FCSTD DOCUMENT  (FreeCAD 0.19R23258 (Git))
Label: star_sketch
License: All rights reserved
LicenseURL: http://en.wikipedia.org/wiki/All_rights_reserved
objects: Sketcher::SketchObject×2
note: 2 computed .brp shape members not serialized (recipe doc carries the construction recipe); baked Part::Feature solids carry a one-line shape summary decoded from their .brp

FEATURE [Sketcher::SketchObject] Sketch
  sketch-geometry (31):
    g0: LineSegment [constr] StartX=0 StartY=15.4617 StartZ=0 EndX=-14.705 EndY=4.77794 EndZ=0
    g1: LineSegment [constr] StartX=-14.705 StartY=4.77794 StartZ=0 EndX=-9.08818 EndY=-12.5088 EndZ=0
    g2: LineSegment [constr] StartX=-9.08818 StartY=-12.5088 StartZ=0 EndX=9.08818 EndY=-12.5088 EndZ=0
    g3: LineSegment [constr] StartX=9.08818 StartY=-12.5088 StartZ=0 EndX=14.705 EndY=4.77794 EndZ=0
    g4: LineSegment [constr] StartX=14.705 StartY=4.77794 StartZ=0 EndX=0 EndY=15.4617 EndZ=0
    g5: Circle [constr] CenterX=0 CenterY=0 CenterZ=0 NormalX=0 NormalY=0 NormalZ=1 AngleXU=0 Radius=15.4617
    g6: LineSegment [constr] StartX=0 StartY=0 StartZ=0 EndX=0 EndY=40 EndZ=0
    g7: LineSegment [constr] StartX=0 StartY=0 StartZ=0 EndX=38.0423 EndY=12.3607 EndZ=0
    g8: LineSegment [constr] StartX=0 StartY=0 StartZ=0 EndX=23.5114 EndY=-32.3607 EndZ=0
    g9: LineSegment [constr] StartX=0 StartY=0 StartZ=0 EndX=-23.5114 EndY=-32.3607 EndZ=0
    g10: LineSegment [constr] StartX=0 StartY=0 StartZ=0 EndX=-38.0423 EndY=12.3607 EndZ=0
    g11: LineSegment StartX=0 StartY=40 StartZ=0 EndX=10.6055 EndY=14.5972 EndZ=0
    g12: LineSegment StartX=0 StartY=40 StartZ=0 EndX=-10.6055 EndY=14.5972 EndZ=0
    g13: LineSegment StartX=-38.0423 StartY=12.3607 StartZ=0 EndX=-17.1601 EndY=-5.57564 EndZ=0
    g14: LineSegment StartX=-38.0423 StartY=12.3607 StartZ=0 EndX=-10.6055 EndY=14.5972 EndZ=0
    g15: LineSegment StartX=-23.5114 StartY=-32.3607 StartZ=0 EndX=0 EndY=-18.0432 EndZ=0
    g16: LineSegment StartX=-14.705 StartY=4.77794 StartZ=0 EndX=-15.2847 EndY=2.3333 EndZ=0
    g17: LineSegment StartX=23.5114 StartY=-32.3607 StartZ=0 EndX=17.1601 EndY=-5.57564 EndZ=0
    g18: LineSegment StartX=23.5114 StartY=-32.3607 StartZ=0 EndX=0 EndY=-18.0432 EndZ=0
    g19: LineSegment StartX=0 StartY=15.4617 StartZ=0 EndX=2.50412 EndY=15.2576 EndZ=0
    g20: LineSegment StartX=38.0423 StartY=12.3607 StartZ=0 EndX=17.1601 EndY=-5.57564 EndZ=0
    g21: LineSegment StartX=-13.737 StartY=7.09642 StartZ=0 EndX=-14.705 EndY=4.77794 EndZ=0
    g22: LineSegment StartX=-2.50412 StartY=15.2576 StartZ=0 EndX=0 EndY=15.4617 EndZ=0
    g23: LineSegment StartX=-17.1601 StartY=-5.57564 StartZ=0 EndX=-23.5114 EndY=-32.3607 EndZ=0
    g24: LineSegment StartX=-10.9941 StartY=-10.8718 StartZ=0 EndX=-9.08818 EndY=-12.5088 EndZ=0
    g25: LineSegment StartX=-6.94232 StartY=-13.8155 StartZ=0 EndX=-9.08818 EndY=-12.5088 EndZ=0
    g26: LineSegment StartX=6.94232 StartY=-13.8155 StartZ=0 EndX=9.08818 EndY=-12.5088 EndZ=0
    g27: LineSegment StartX=10.9941 StartY=-10.8718 StartZ=0 EndX=9.08818 EndY=-12.5088 EndZ=0
    g28: LineSegment StartX=10.6055 StartY=14.5972 StartZ=0 EndX=38.0423 EndY=12.3607 EndZ=0
    g29: LineSegment StartX=15.2847 StartY=2.3333 StartZ=0 EndX=14.705 EndY=4.77794 EndZ=0
    g30: LineSegment StartX=13.737 StartY=7.09642 StartZ=0 EndX=14.705 EndY=4.77794 EndZ=0
  constraints (73):
    c: Coincident(g0,g1)
    c: Coincident(g1,g2)
    c: Coincident(g2,g3)
    c: Coincident(g3,g4)
    c: Coincident(g4,g0)
    c: Equal(g0, g1-g4) x4
    c: PointOnObject(g0,g5)
    c: PointOnObject(g1,g5)
    c: PointOnObject(g2,g5)
    c: PointOnObject(g3,g5)
    c: PointOnObject(g4,g5)
    c: Coincident(g5,g-1)
    c: PointOnObject(g4,g-2)
    c: Coincident(g6,g-1)
    c: PointOnObject(g6,g-2)
    c: Distance(g6) = 40
    c: Coincident(g7,g6)
    c: PointOnObject(g3,g7)
    c: Distance(g7) = 40
    c: Coincident(g8,g6)
    c: PointOnObject(g2,g8)
    c: Distance(g8) = 40
    c: Coincident(g9,g6)
    c: PointOnObject(g1,g9)
    c: Distance(g9) = 40
    c: Coincident(g10,g6)
    c: PointOnObject(g0,g10)
    c: Distance(g10) = 40
    c: Coincident(g11,g6)
    c: Coincident(g30,g3)
    c: Coincident(g12,g6)
    c: Coincident(g21,g0)
    c: Coincident(g13,g10)
    c: Coincident(g14,g10)
    c: Coincident(g24,g1)
    c: Coincident(g22,g0)
    c: Coincident(g15,g9)
    c: Coincident(g23,g9)
    c: Coincident(g16,g0)
    c: Coincident(g26,g2)
    c: Coincident(g18,g8)
    c: Coincident(g17,g8)
    c: Coincident(g25,g1)
    c: Coincident(g29,g3)
    c: Coincident(g28,g7)
    c: Coincident(g20,g7)
    c: Coincident(g19,g0)
    c: Coincident(g27,g2)
    c: PointOnObject(g21,g5)
    c: Tangent(g12,g21)
    c: Coincident(g14,g12)
    c: PointOnObject(g22,g5)
    c: Tangent(g14,g22)
    c: PointOnObject(g16,g5)
    c: Tangent(g16,g23)
    c: Coincident(g13,g23)
    c: PointOnObject(g24,g5)
    c: Tangent(g13,g24)
    c: PointOnObject(g25,g5)
    c: Tangent(g18,g25)
    c: Coincident(g15,g18)
    c: PointOnObject(g26,g5)
    c: Tangent(g15,g26)
    c: PointOnObject(g27,g5)
    c: Tangent(g20,g27)
    c: PointOnObject(g19,g5)
    c: Tangent(g19,g28)
    c: Coincident(g17,g20)
    c: PointOnObject(g29,g5)
    c: Tangent(g17,g29)
    c: Coincident(g11,g28)
    c: PointOnObject(g30,g5)
    c: Tangent(g11,g30)
FEATURE [Sketcher::SketchObject] Sketch001
  sketch-geometry (2):
    g0: LineSegment [constr] StartX=-10.6191 StartY=14.4725 StartZ=0 EndX=10.7361 EndY=14.4725 EndZ=0
    g1: LineSegment [constr] StartX=17.097 StartY=-5.65805 StartZ=0 EndX=10.7361 EndY=14.4725 EndZ=0
  constraints (2):
    c: Horizontal(g0)
    c: Coincident(g1,g0)
